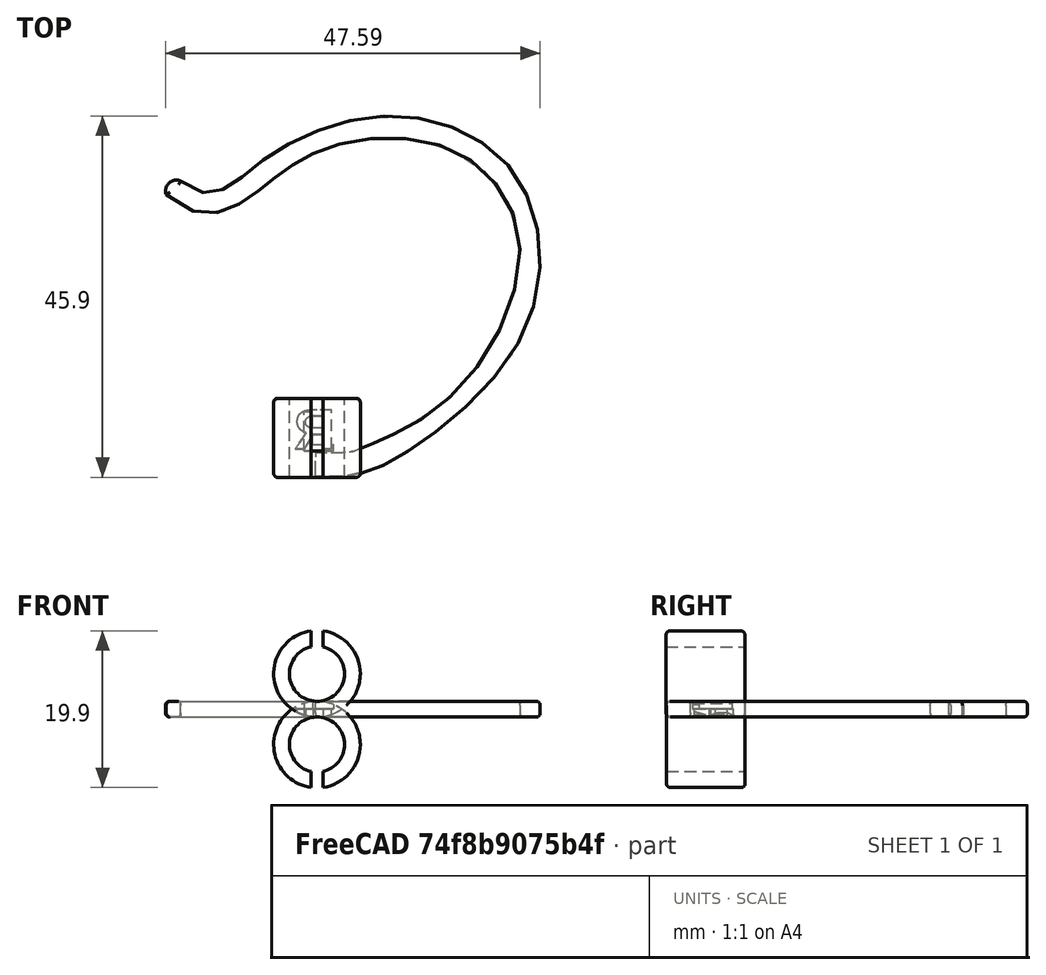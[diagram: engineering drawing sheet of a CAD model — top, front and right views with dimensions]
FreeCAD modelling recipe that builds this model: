
FCSTD DOCUMENT  (FreeCAD 1.0R39319 (Git))
Label: inear headset bt fix
License: All rights reserved
LicenseURL: https://en.wikipedia.org/wiki/All_rights_reserved
objects: PartDesign::Fillet×3, PartDesign::Body×3, PartDesign::AdditiveCylinder×2, PartDesign::SubtractiveCylinder×2, PartDesign::SubtractiveBox×2, Part::Part2DObjectPython×2, PartDesign::Pocket×2, Mesh::Feature×1, Sketcher::SketchObject×1, PartDesign::Pad×1
note: 43 computed .brp shape members not serialized (recipe doc carries the construction recipe); baked Part::Feature solids carry a one-line shape summary decoded from their .brp

FEATURE [Mesh::Feature] EarBud_Hook_SG7
FEATURE [Sketcher::SketchObject] Sketch
  ArcFitTolerance = 1e-06
  AttachmentSupport = -> [XY_Plane]
  FullyConstrained = true
  MakeInternals = false
  MapMode = 5
  sketch-geometry (38):
    g0-g9: Circle [constr] x10 (B-spline internal-alignment scaffolding for g10; pole/knot coordinates omitted)
    g10: BSplineCurve PolesCount=10 KnotsCount=8 Degree=3 IsPeriodic=0
    g11-g18: GeomPoint [constr] x8 (B-spline internal-alignment scaffolding for g10; pole/knot coordinates omitted)
    g19-g27: Circle [constr] x9 (B-spline internal-alignment scaffolding for g28; pole/knot coordinates omitted)
    g28: BSplineCurve PolesCount=9 KnotsCount=7 Degree=3 IsPeriodic=0
    g29-g35: GeomPoint [constr] x7 (B-spline internal-alignment scaffolding for g28; pole/knot coordinates omitted)
    g36: LineSegment StartX=21.8 StartY=7 StartZ=0 EndX=21.8 EndY=10 EndZ=0
    g37: ArcOfCircle CenterX=4.15 CenterY=43.2786 CenterZ=0 NormalX=0 NormalY=0 NormalZ=1 AngleXU=0 Radius=1.38529 StartAngle=1.16252 EndAngle=3.49433
  constraints (51):
    c: Weight(g0) = 1
    c: Equal(g0, g1-g9) x9
    c: InternalAlignment(g0-g9 -> g10) x10
    c: InternalAlignment(g11-g18 -> g10) x8
    c: DistanceX(g-1,g10) = 21.8
    c: DistanceY(g-1,g10) = 10
    c: DistanceX(g-1,g7) = 25.15
    c: DistanceX(g-1,g8) = 27.25
    c: DistanceY(g-1,g7) = 10
    c: DistanceY(g-1,g8) = 10
    c: DistanceY(g-1,g10) = 42.8
    c: Distance(g10,g-2) = 2.85
    c: Distance(g12,g-2) = 13.9
    c: DistanceY(g-1,g12) = 42.8
    c: DistanceY(g-1,g13) = 48.65
    c: Distance(g13,g-2) = 23
    c: DistanceX(g-1,g14) = 38.4
    c: DistanceY(g-1,g14) = 48.8
    c: DistanceY(g-1,g15) = 36.1
    c: Distance(g15,g-2) = 47.75
    c: Distance(g16,g-2) = 40
    c: DistanceY(g-1,g16) = 18.15
    c: DistanceY(g-1,g1) = 38.75
    c: Distance(g5,g-2) = 51.55
    c: Weight(g19) = 1
    c: Equal(g19, g20-g27) x8
    c: InternalAlignment(g19-g27 -> g28) x9
    c: InternalAlignment(g29-g35 -> g28) x7
    c: DistanceX(g-1,g28) = 21.8
    c: DistanceY(g-1,g28) = 7
    c: DistanceY(g-1,g34) = 10.75
    c: DistanceX(g-1,g34) = 34.4
    c: DistanceX(g-1,g33) = 48.5
    c: DistanceY(g-1,g33) = 25.8
    c: DistanceY(g-1,g32) = 45
    c: DistanceX(g-1,g32) = 47.4
    c: DistanceX(g-1,g31) = 31.8
    c: DistanceY(g-1,g31) = 52.8
    c: DistanceX(g-1,g30) = 15.6
    c: DistanceY(g-1,g30) = 47.5
    c: DistanceX(g-1,g28) = 4.7
    c: DistanceY(g-1,g28) = 44.55
    c: DistanceX(g-1,g20) = 9
    c: DistanceX(g-1,g22) = 31.7
    c: DistanceY(g-1,g23) = 47.5
    c: DistanceY(g-1,g24) = 24.69
    c: Coincident(g36,g10)
    c: Coincident(g28,g36)
    c: Coincident(g37,g10)
    c: Coincident(g37,g28)
    c: DistanceX(g-1,g37) = 4.15
FEATURE [PartDesign::Pad] Pad
  Direction = (0,0,1)
  Length = 2
  Length2 = 10
  Profile = -> Sketch
  ReferenceAxis = -> Sketch [N_Axis]
  Refine = true
  Suppressed = false
  Type = 0
FEATURE [PartDesign::AdditiveCylinder] Cylinder
  Angle = 360
  AttacherType = Attacher::AttachEngine3D
  AttachmentOffset = pos=(22,5.5,-10) rot=(0,0,1;0rad)
  AttachmentSupport = -> [XZ_Plane001]
  FirstAngle = 0
  Height = 10
  MapMode = 5
  Placement = pos=(22,10,5.5) rot=(1,0,0;1.5708rad)
  Radius = 5.5
  Refine = true
  SecondAngle = 0
  Suppressed = false
FEATURE [PartDesign::SubtractiveCylinder] Cylinder001
  Angle = 360
  AttacherType = Attacher::AttachEngine3D
  AttachmentOffset = pos=(22,5.5,-10) rot=(0,0,1;0rad)
  AttachmentSupport = -> [XZ_Plane001]
  BaseFeature = -> Cylinder
  FirstAngle = 0
  Height = 10
  MapMode = 5
  Placement = pos=(22,10,5.5) rot=(1,0,0;1.5708rad)
  Radius = 3.5
  Refine = true
  SecondAngle = 0
  Suppressed = false
FEATURE [PartDesign::SubtractiveBox] Box
  AttacherType = Attacher::AttachEngine3D
  AttachmentOffset = pos=(21.25,4,-10) rot=(0,0,1;0rad)
  AttachmentSupport = -> [XZ_Plane001]
  BaseFeature = -> Cylinder001
  Height = 10
  Length = 1.5
  MapMode = 5
  Placement = pos=(21.25,10,4) rot=(1,0,0;1.5708rad)
  Refine = true
  Suppressed = false
  Width = 10
FEATURE [PartDesign::Fillet] Fillet
  Base = -> Pad [Edge12,Edge7,Edge6,Edge11,Edge3,Edge4]
  BaseFeature = -> Pad
  Radius = 0.5
  Refine = true
  SupportTransform = false
  Suppressed = false
  UseAllEdges = false
FEATURE [PartDesign::Body] Body  label="ear shape"
  AllowCompound = false
  Group = -> [Sketch,Pad,Fillet]
  Origin = -> Origin
  Tip = -> Fillet
FEATURE [PartDesign::Fillet] Fillet001
  Base = -> Box [Edge14,Edge6]
  BaseFeature = -> Box
  Placement = pos=(21.25,10,4) rot=(1,0,0;1.5708rad)
  Radius = 0.5
  Refine = true
  SupportTransform = false
  Suppressed = false
  UseAllEdges = false
FEATURE [Part::Part2DObjectPython] ShapeString  # Draft 2D object (typed FeaturePython)
  FontFile = <path>
  Fuse = false
  Justification = 6
  JustificationReference = 0
  KeepLeftMargin = false
  MakeFace = true
  ObliqueAngle = 0
  Placement = pos=(23.86,3.58,1.3e-15) rot=(0,1,0;3.14159rad)
  ScaleToSize = true
  Size = 5
  String = R
  Tracking = 0
FEATURE [PartDesign::Pocket] Pocket
  BaseFeature = -> Fillet001
  Direction = (-1e-16,2e-16,1)
  Length = 1
  Length2 = 5
  Placement = pos=(21.25,10,4) rot=(1,0,0;1.5708rad)
  Profile = -> ShapeString
  ReferenceAxis = -> ShapeString [N_Axis]
  Refine = true
  Suppressed = false
  Type = 0
FEATURE [PartDesign::Body] Body001  label="Right"
  AllowCompound = false
  Group = -> [Cylinder,Cylinder001,Box,Fillet001,ShapeString,Pocket]
  Origin = -> Origin001
  Placement = pos=(0,6.9,0) rot=(0,0,1;0rad)
  Tip = -> Pocket
FEATURE [PartDesign::AdditiveCylinder] Cylinder002
  Angle = 360
  AttacherType = Attacher::AttachEngine3D
  AttachmentOffset = pos=(22,-3.5,-16.9) rot=(0,0,1;0rad)
  AttachmentSupport = -> [XZ_Plane002]
  FirstAngle = 0
  Height = 10
  MapMode = 5
  Placement = pos=(22,16.9,-3.5) rot=(1,0,0;1.5708rad)
  Radius = 5.5
  Refine = true
  SecondAngle = 0
  Suppressed = false
FEATURE [PartDesign::SubtractiveCylinder] Cylinder003
  Angle = 360
  AttacherType = Attacher::AttachEngine3D
  AttachmentOffset = pos=(22,-3.5,-17) rot=(0,0,1;0rad)
  AttachmentSupport = -> [XZ_Plane002]
  BaseFeature = -> Cylinder002
  FirstAngle = 0
  Height = 10.1
  MapMode = 5
  Placement = pos=(22,17,-3.5) rot=(1,0,0;1.5708rad)
  Radius = 3.5
  Refine = true
  SecondAngle = 0
  Suppressed = false
FEATURE [PartDesign::SubtractiveBox] Box001
  AttacherType = Attacher::AttachEngine3D
  AttachmentOffset = pos=(21.25,-9,-17.5) rot=(0,0,1;0rad)
  AttachmentSupport = -> [XZ_Plane002]
  BaseFeature = -> Cylinder003
  Height = 11
  Length = 1.5
  MapMode = 5
  Placement = pos=(21.25,17.5,-9) rot=(1,0,0;1.5708rad)
  Refine = true
  Suppressed = false
  Width = 8
FEATURE [PartDesign::Fillet] Fillet002
  Base = -> Box001 [Edge14,Edge6]
  BaseFeature = -> Box001
  Placement = pos=(21.25,17.5,-9) rot=(1,0,0;1.5708rad)
  Radius = 0.5
  Refine = true
  SupportTransform = false
  Suppressed = false
  UseAllEdges = false
FEATURE [Part::Part2DObjectPython] ShapeString001  # Draft 2D object (typed FeaturePython)
  FontFile = <path>
  Fuse = false
  Justification = 6
  JustificationReference = 0
  KeepLeftMargin = false
  MakeFace = true
  ObliqueAngle = 0
  Placement = pos=(20.37,10.21,2.01) rot=(0,0,1;0rad)
  ScaleToSize = true
  Size = 5
  String = L
  Tracking = 0
FEATURE [PartDesign::Pocket] Pocket001
  BaseFeature = -> Fillet002
  Direction = (0,0,-1)
  Length = 1
  Length2 = 5
  Placement = pos=(21.25,17.5,-9) rot=(1,0,0;1.5708rad)
  Profile = -> ShapeString001
  ReferenceAxis = -> ShapeString001 [N_Axis]
  Refine = true
  Suppressed = false
  Type = 0
FEATURE [PartDesign::Body] Body002  label="Left"
  AllowCompound = false
  Group = -> [Cylinder002,Cylinder003,Box001,Fillet002,ShapeString001,Pocket001]
  Origin = -> Origin002
  Placement = pos=(0,0.04,0) rot=(0,0,1;0rad)
  Tip = -> Pocket001
note: 2 file-system paths scrubbed to <path> (originals preserved in the JSON sidecar)
